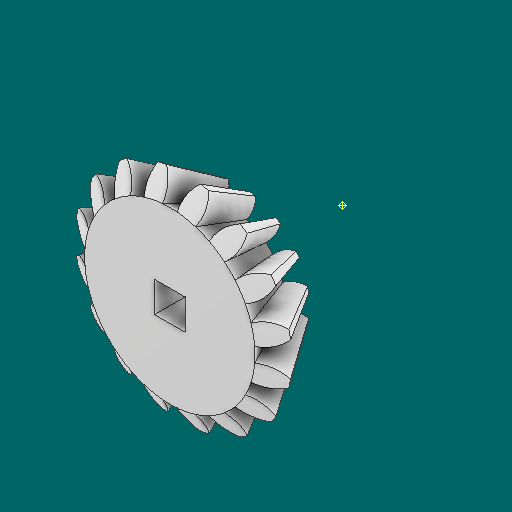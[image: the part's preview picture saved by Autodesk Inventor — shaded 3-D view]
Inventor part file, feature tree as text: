
AUTODESK INVENTOR PART (.ipt)
format: ipt  version: 2023.1 (Build 271208000, 208)  size: 492,032 bytes
history: native  units: in
note: dims shown in document units (in); Inventor stores cm internally (conversion verified against a paired STEP export)
features: other x30, sketch x2
ambient origin geometry x8: Origin, YZ Plane, XZ Plane, XY Plane, X Axis, Y Axis, Z Axis, Center Point
bodies: Solid1 (feature_tree)
feature tree (32):
  other  "Bevel Gear1"
  other  "Solid1::Bevel Gear1"
  other  "TaggingFeature1"
  other  "Teeth Body Sketch"
  other  "Start Sketch"
  other  "End Sketch"
  other  "End Sketch Right"
  other  "End Sketch Left"
  other  "Body Sketch"
  sketch  "Sketch6"  dims[d0=0.3937in]
  sketch  "Sketch8"  dims[d48=0.0in d49=0.0in d50=90.0deg d52=0.0in d53=0.0in d54=0.0in]
  other  "3D Sketch Right"
  other  "3D Sketch Left"
  other  "Mesh Plane"
  other  "Top Plane"
  other  "Mesh Plane2"
  other  "Tooth Plane"
  other  "End Plane"
  other  "End Plane Right"
  other  "End Plane Left"
  other  "Z Axis_1"
  other  "Top Point"
  other  "Start Point"
  other  "End Point"
  other  "Srf1"
  other  "Srf1::Derived"
  other  "Start plane iMate"
  other  "Mesh iMate2"
  other  "Axis Angle iMate"
  other  "Axis iMate"
  other  "Mesh iMate"
  other  "Intersection iMate"
